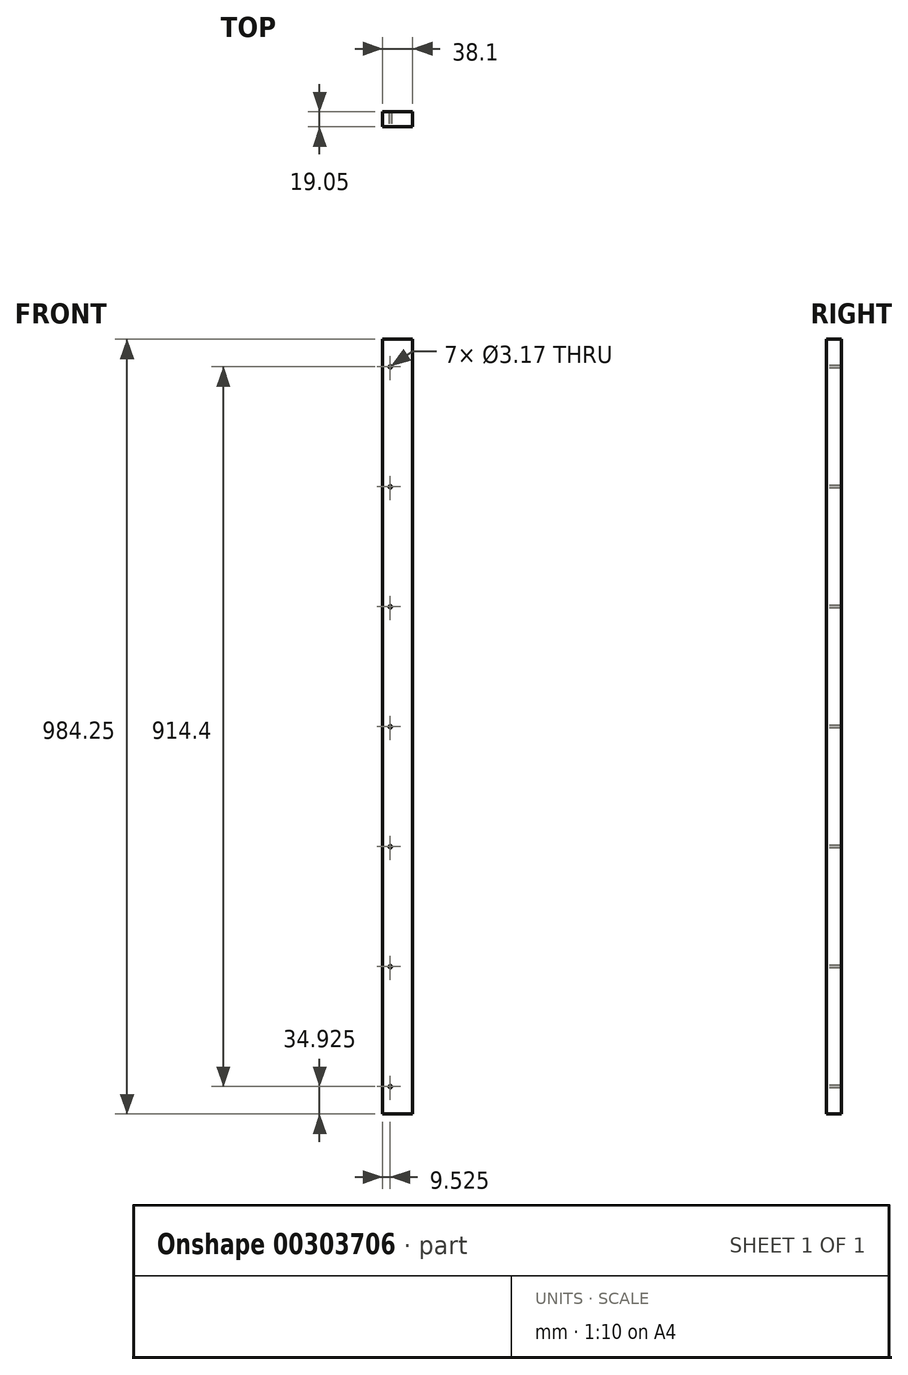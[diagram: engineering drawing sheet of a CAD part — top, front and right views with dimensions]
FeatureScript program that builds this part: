
annotation { "Feature Type Name" : "Feature", "Feature Type Description" : "" }
export const myFeature = defineFeature(function(context is Context, id is Id, definition is map)
    precondition{}
    {
        {
            var Q0;
            Q0=qCreatedBy(makeId("Front.planeOp"),FACE);
            var sketch = newSketch(context, id + "F0", { "sketchPlane" : qUnion([Q0])});
            skLineSegment(sketch, "E0.bottom", {"start": v(0, 0) * mm, "end": v(38.1, 0) * mm});
            skLineSegment(sketch, "E0.top", {"start": v(0, -984.25) * mm, "end": v(38.1, -984.25) * mm});
            skLineSegment(sketch, "E0.left", {"start": v(0, 0) * mm, "end": v(0, -984.25) * mm});
            skLineSegment(sketch, "E0.right", {"start": v(38.1, 0) * mm, "end": v(38.1, -984.25) * mm});
            skSolve(sketch);
        }
        {
            var Q0;
            Q0 = qSketchRegion(id + "F0", true);
            extrude(context, id + "F1", {"entities" : qUnion([Q0]), "oppositeDirection" : true, "depth" : 19.05 * mm});
        }
        {
            var Q0;
            Q0=qCreatedBy(makeId("Front.planeOp"),FACE);
            var sketch = newSketch(context, id + "F2", { "sketchPlane" : qUnion([Q0])});
            skCircle(sketch, "E1", {"center": v(9.52, -34.92) * mm, "radius": 1.59 * mm});
            skCircle(sketch, "E2.1.0.0", {"center": v(9.52, -187.32) * mm, "radius": 1.59 * mm});
            skCircle(sketch, "E2.2.0.0", {"center": v(9.52, -339.73) * mm, "radius": 1.59 * mm});
            skCircle(sketch, "E2.3.0.0", {"center": v(9.52, -492.13) * mm, "radius": 1.59 * mm});
            skCircle(sketch, "E2.4.0.0", {"center": v(9.52, -644.53) * mm, "radius": 1.59 * mm});
            skCircle(sketch, "E2.5.0.0", {"center": v(9.52, -796.93) * mm, "radius": 1.59 * mm});
            skLineSegment(sketch, "E2.direction1", {"start": v(9.52, -34.92) * mm, "end": v(9.52, -187.32) * mm, "construction": true});
            skCircle(sketch, "E3.0.6.0", {"center": v(9.52, -949.33) * mm, "radius": 1.59 * mm});
            skSolve(sketch);
        }
        {
            var Q0;
            Q0 = qSketchRegion(id + "F2", true);
            extrude(context, id + "F3", {"entities" : qUnion([Q0]), "operationType" : NewBodyOperationType.REMOVE, "endBound" : BoundingType.THROUGH_ALL, "oppositeDirection" : true, "depth" : 25.4 * mm});
        }
    });
